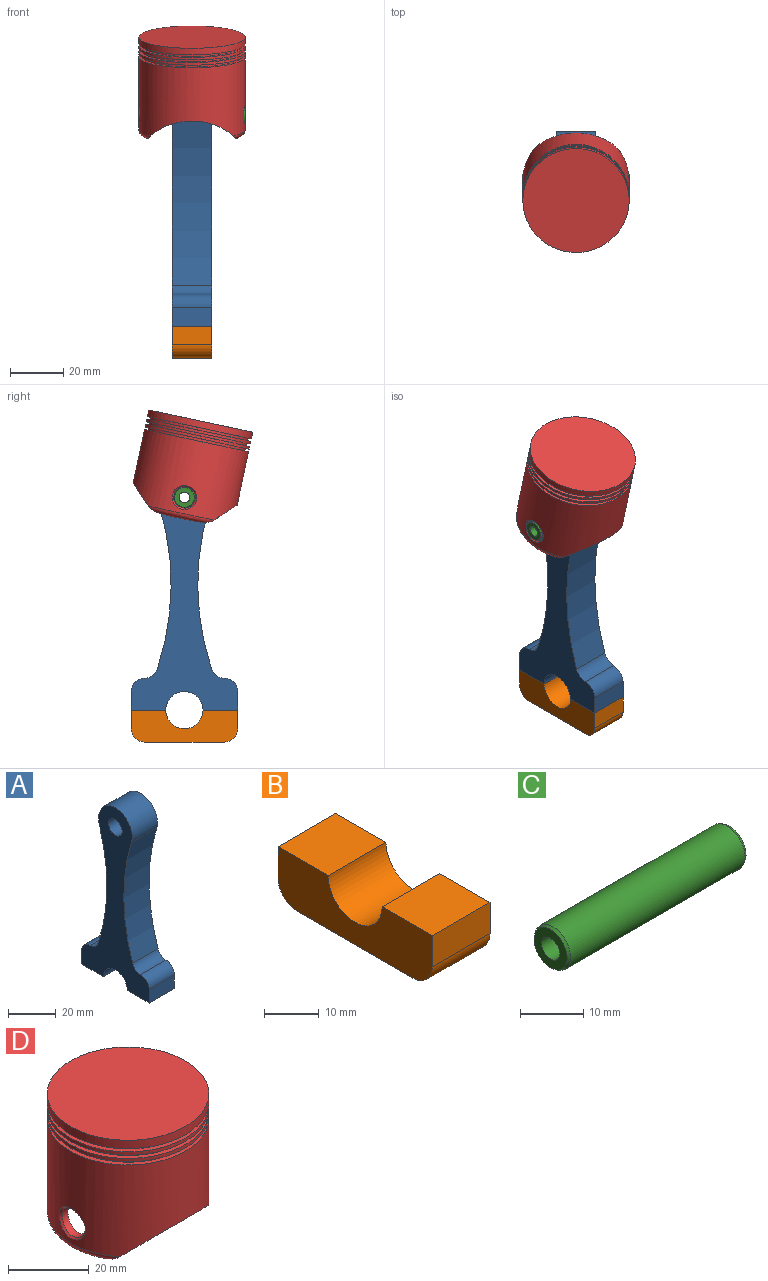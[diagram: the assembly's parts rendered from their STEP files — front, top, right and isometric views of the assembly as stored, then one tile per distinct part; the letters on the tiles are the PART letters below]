
ASSEMBLY  parts=4 mates=3
PART A: 15 faces, bbox 15x40x90 mm
  f0: plane 15x7mm, normal (0,-1,0), area 105mm2, adj f1,f11,f13,f14
  f1: plane 15x13mm, normal (0,0,-1), area 195mm2, adj f0,f2,f13,f14
  f2: cylinder r=7mm len=15mm, axis (-1,0,0), area 329.9mm2, adj f1,f3,f13,f14
  f3: plane 15x13mm, normal (0,0,-1), area 195mm2, adj f2,f4,f13,f14
  f4: plane 15x7mm, normal (0,1,0), area 105mm2, adj f3,f5,f13,f14
  f5: cylinder r=5mm len=15mm, axis (-1,0,0), area 117.8mm2, adj f4,f6,f13,f14
  f6: cylinder r=5mm len=15mm, axis (-1,0,0), area 93.3mm2, adj f5,f7,f13,f14
  f7: cylinder r=99.37mm len=61.62mm, axis (-1,0,0), area 939.8mm2, adj f6,f8,f13,f14
  f8: cylinder r=10mm len=20mm, axis (-1,0,0), area 562.3mm2, adj f7,f9,f13,f14
  f9: cylinder r=99.37mm len=61.62mm, axis (-1,0,0), area 939.8mm2, adj f8,f10,f13,f14
  f10: cylinder r=5mm len=15mm, axis (-1,0,0), area 93.3mm2, adj f9,f11,f13,f14
  f11: cylinder r=5mm len=15mm, axis (-1,0,0), area 117.8mm2, adj f0,f10,f13,f14
  f12: cylinder r=4mm len=15mm, axis (-1,0,0), area 377mm2, adj f13,f14
  f13: plane 90x40mm, normal (1,0,0), area 1452.4mm2, adj f0,f1,f2,f3,f4,f5,f6,f7
  f14: plane 90x40mm, normal (-1,0,0), area 1452.4mm2, adj f0,f1,f2,f3,f4,f5,f6,f7
PART B: 10 faces, bbox 15x40x12 mm
  f0: cylinder r=7mm len=15mm, axis (-1,0,0), area 329.9mm2, adj f1,f7,f8,f9
  f1: plane 15x13mm, normal (0,0,1), area 195mm2, adj f0,f2,f8,f9
  f2: plane 15x7mm, normal (0,-1,0), area 105mm2, adj f1,f3,f8,f9
  f3: cylinder r=5mm len=15mm, axis (-1,0,0), area 117.8mm2, adj f2,f4,f8,f9
  f4: plane 30x15mm, normal (0,0,-1), area 450mm2, adj f3,f5,f8,f9
  f5: cylinder r=5mm len=15mm, axis (-1,0,0), area 117.8mm2, adj f4,f6,f8,f9
  f6: plane 15x7mm, normal (0,1,0), area 105mm2, adj f5,f7,f8,f9
  f7: plane 15x13mm, normal (0,0,1), area 195mm2, adj f0,f6,f8,f9
  f8: plane 40x12mm, normal (1,0,0), area 392.3mm2, adj f0,f1,f2,f3,f4,f5,f6,f7
  f9: plane 40x12mm, normal (-1,0,0), area 392.3mm2, adj f0,f1,f2,f3,f4,f5,f6,f7
PART C: 6 faces, bbox 40x8x8 mm
  f0: cylinder r=2mm len=40mm, axis (-1,0,0), area 502.7mm2, adj f1,f3
  f1: plane 7.42x7.42mm, normal (1,0,0), area 30.7mm2, adj f0,f5
  f2: cylinder r=4mm len=39mm, axis (-1,0,0), area 980.2mm2, adj f4,f5
  f3: plane 7.42x7.42mm, normal (-1,0,0), area 30.7mm2, adj f0,f4
  f4: cone r=3.71mm half-angle=30deg, axis (1,0,0), area 14mm2, adj f2,f3
  f5: cone r=4mm half-angle=30deg, axis (-1,0,0), area 14mm2, adj f1,f2
PART D: 28 faces, bbox 43.3x40x37.4 mm
  f0: cylinder r=20mm len=32.73mm, axis (0,-1,0), area 120mm2, adj f1,f10,f11,f12,f26,f27
  f1: cylinder r=17.5mm len=35mm, axis (0,0,-1), area 2930.5mm2, adj f0,f2,f4,f6,f7,f8,f10,f27
  f2: cylinder r=4mm len=8mm, axis (1,0,0), area 50.3mm2, adj f1,f3
  f3: bspline ~9.23x8.99mm, area 20.1mm2, adj f2,f12
  f4: cylinder r=4mm len=8mm, axis (1,0,0), area 50.3mm2, adj f1,f5
  f5: bspline ~9.23x9mm, area 20.1mm2, adj f4,f12
  f6: cylinder r=2mm len=16.08mm, axis (0,-1,0), area 35.3mm2, adj f1,f7,f26
  f7: cylinder r=20mm len=32.73mm, axis (0,-1,0), area 120mm2, adj f1,f6,f10,f11,f12,f26
  f8: torus R=15mm, axis (0,0,1), area 409.4mm2, adj f1,f9
  f9: plane 30x30mm, normal (0,0,-1), area 706.9mm2, adj f8
  f10: cylinder r=2mm len=21.71mm, axis (0,-1,0), area 108.5mm2, adj f0,f1,f7,f11
  f11: torus R=18mm, axis (0,0,-1), area 52.5mm2, adj f0,f7,f10,f12
  f12: cylinder r=20mm len=40mm, axis (0,0,-1), area 3026.1mm2, adj f0,f3,f5,f7,f11,f13,f26
  f13: plane 40x40mm, normal (0,0,1), area 152.2mm2, adj f12,f14
  f14: cylinder r=18.75mm len=37.5mm, axis (0,0,-1), area 117.8mm2, adj f13,f15
  f15: plane 40x40mm, normal (0,0,-1), area 152.2mm2, adj f14,f16
  f16: cylinder r=20mm len=40mm, axis (0,0,-1), area 125.7mm2, adj f15,f17
  f17: plane 40x40mm, normal (0,0,1), area 152.2mm2, adj f16,f18
  f18: cylinder r=18.75mm len=37.5mm, axis (0,0,-1), area 117.8mm2, adj f17,f19
  f19: plane 40x40mm, normal (0,0,-1), area 152.2mm2, adj f18,f20
  f20: cylinder r=20mm len=40mm, axis (0,0,-1), area 125.7mm2, adj f19,f21
  f21: plane 40x40mm, normal (0,0,1), area 152.2mm2, adj f20,f22
  f22: cylinder r=18.75mm len=37.5mm, axis (0,0,-1), area 117.8mm2, adj f21,f23
  f23: plane 40x40mm, normal (0,0,-1), area 152.2mm2, adj f22,f24
  f24: cylinder r=20mm len=40mm, axis (0,0,-1), area 314.2mm2, adj f23,f25
  f25: plane 40x40mm, normal (0,0,1), area 1256.6mm2, adj f24
  f26: torus R=18mm, axis (0,0,-1), area 52.5mm2, adj f0,f6,f7,f12,f27
  f27: cylinder r=2mm len=5.63mm, axis (0,-1,0), area 2.3mm2, adj f0,f1,f26
PLACE A t=(0,0,36.35)mm
PLACE B t=(0,0,36.35)mm
PLACE C t=(0,0,36.35)mm
PLACE D rot(axis=(1,0,0),12.1deg) t=(-0.01,11.66,37.59)mm
MATE revolute A.f8 <-> C.f0  axis (-1,0,0) through (0,0,92)mm
MATE fastened B.f0 <-> A.f2  axis (-1,0,0) through (0,0,12)mm
MATE revolute D.f2 <-> C.f0  axis (1,0,0) through (19.5,0,92)mm
